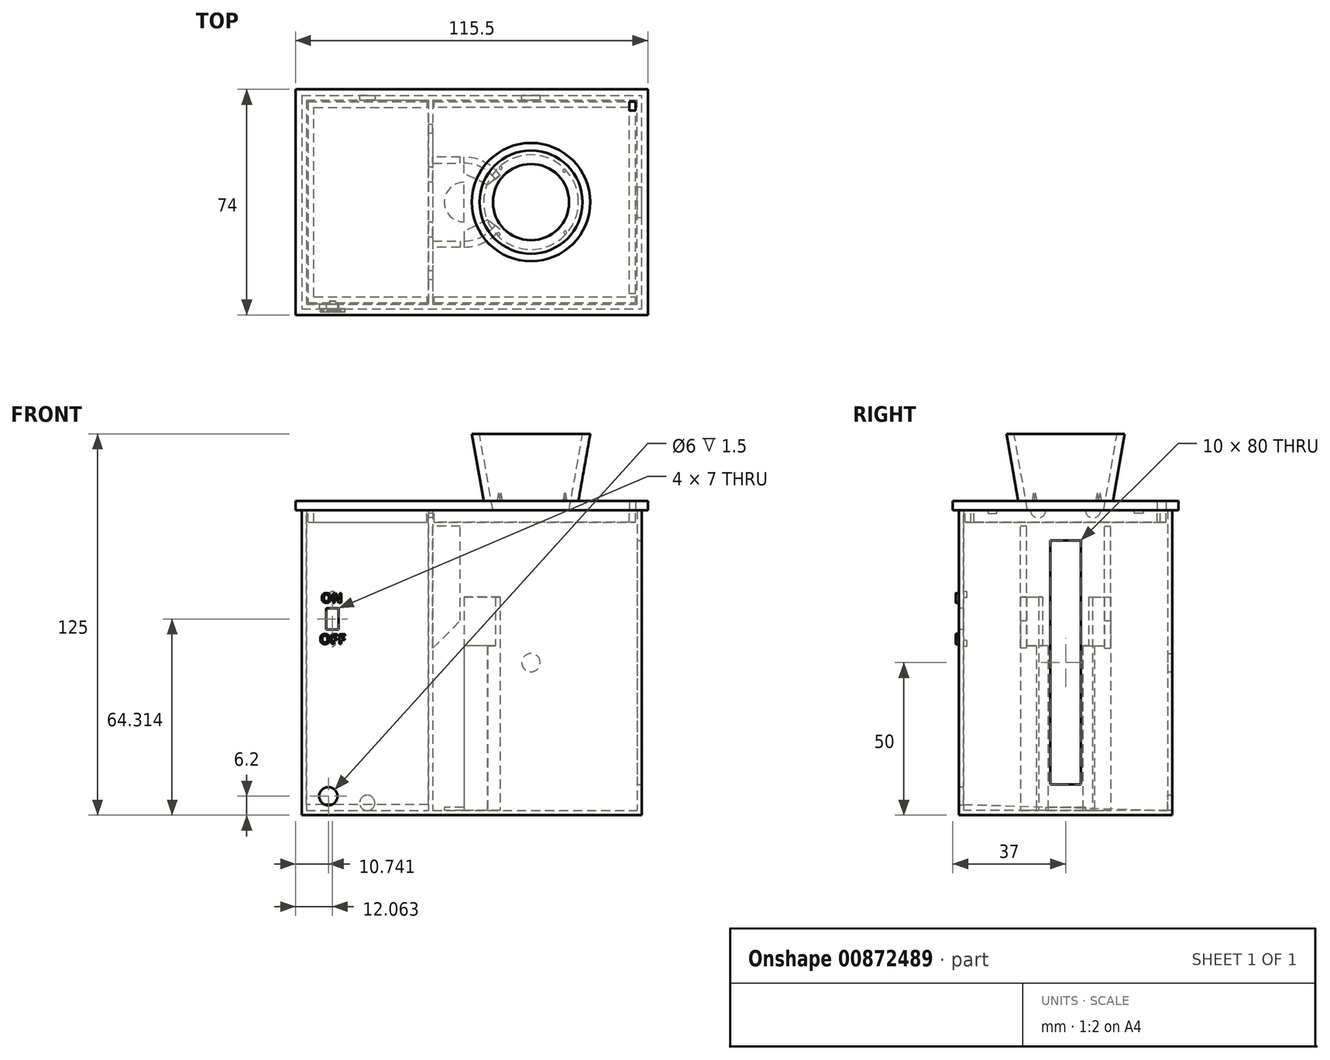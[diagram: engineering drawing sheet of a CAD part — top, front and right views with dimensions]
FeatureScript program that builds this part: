
annotation { "Feature Type Name" : "Feature", "Feature Type Description" : "" }
export const myFeature = defineFeature(function(context is Context, id is Id, definition is map)
    precondition{}
    {
        {
            var Q0;
            Q0=qCreatedBy(makeId("Top.planeOp"),FACE);
            var sketch = newSketch(context, id + "F0", { "sketchPlane" : qUnion([Q0])});
            skLineSegment(sketch, "E0.bottom", {"start": v(-33.7, 35) * mm, "end": v(36.3, 35) * mm});
            skLineSegment(sketch, "E0.left", {"start": v(-33.7, 35) * mm, "end": v(-33.7, 0) * mm});
            skLineSegment(sketch, "E0.right", {"start": v(36.3, 35) * mm, "end": v(36.3, 0) * mm});
            skLineSegment(sketch, "E1.MirrorCS", {"start": v(-33.7, -35) * mm, "end": v(-33.7, 0) * mm});
            skLineSegment(sketch, "E2.MirrorCS", {"start": v(-33.7, -35) * mm, "end": v(36.3, -35) * mm});
            skLineSegment(sketch, "E3.MirrorCS", {"start": v(36.3, -35) * mm, "end": v(36.3, 0) * mm});
            skSolve(sketch);
        }
        {
            var Q0;
            Q0 = qSketchRegion(id + "F0", true);
            extrude(context, id + "F1", {"entities" : qUnion([Q0]), "depth" : 100 * mm, "offsetDistance" : 25 * mm});
        }
        {
            var Q0;
            Q0=makeQuery(id+"F1.opExtrude","CAP_FACE",FACE,{"disambiguationData":[OSD([sQuery(id+"F0.wireOp",EDGE,"E0.bottom"),sQuery(id+"F0.wireOp",EDGE,"E0.left"),sQuery(id+"F0.wireOp",EDGE,"E0.right"),sQuery(id+"F0.wireOp",EDGE,"E1.MirrorCS"),sQuery(id+"F0.wireOp",EDGE,"E2.MirrorCS"),sQuery(id+"F0.wireOp",EDGE,"E3.MirrorCS")])],"isStart":false});
            shell(context, id + "F2", {"entities" : qUnion([Q0]), "thickness" : 1.5 * mm});
        }
        {
            var Q0;
            Q0=makeQuery(id+"F1.opExtrude","SWEPT_FACE",FACE,{"disambiguationData":[OSD([sQuery(id+"F0.wireOp",EDGE,"E0.right"),sQuery(id+"F0.wireOp",EDGE,"E3.MirrorCS")])]});
            var sketch = newSketch(context, id + "F3", { "sketchPlane" : qUnion([Q0])});
            skLineSegment(sketch, "E4", {"start": v(0, 10) * mm, "end": v(5, 10) * mm});
            skLineSegment(sketch, "E5.bottom", {"start": v(5, 10) * mm, "end": v(-5, 10) * mm});
            skLineSegment(sketch, "E5.top", {"start": v(5, 90) * mm, "end": v(-5, 90) * mm});
            skLineSegment(sketch, "E5.left", {"start": v(5, 10) * mm, "end": v(5, 90) * mm});
            skLineSegment(sketch, "E5.right", {"start": v(-5, 10) * mm, "end": v(-5, 90) * mm});
            skSolve(sketch);
        }
        {
            var Q0;
            Q0=makeQuery(id+"F3.imprint","IMPRINT",FACE,{"disambiguationData":[TD([[makeQuery(id+"F3.imprint","IMPRINT",EDGE,{"derivedFrom":sQuery(id+"F3.wireOp",EDGE,"E5.top")}),1.0]])]});
            extrude(context, id + "F4", {"entities" : qUnion([Q0]), "operationType" : NewBodyOperationType.REMOVE, "oppositeDirection" : true, "depth" : 25 * mm, "offsetDistance" : 25 * mm});
        }
        {
            var Q0;
            Q0=makeQuery(id+"F1.opExtrude","SWEPT_FACE",FACE,{"disambiguationData":[OSD([sQuery(id+"F0.wireOp",EDGE,"E0.bottom")])]});
            var sketch = newSketch(context, id + "F5", { "sketchPlane" : qUnion([Q0])});
            skCircle(sketch, "E6", {"center": v(0, 50) * mm, "radius": 3 * mm});
            skSolve(sketch);
        }
        {
            var Q0;
            Q0 = qSketchRegion(id + "F5", true);
            extrude(context, id + "F6", {"entities" : qUnion([Q0]), "operationType" : NewBodyOperationType.REMOVE, "oppositeDirection" : true, "depth" : 25 * mm, "offsetDistance" : 25 * mm});
        }
        {
            var Q0;
            Q0=makeQuery(id+"F1.opExtrude","SWEPT_FACE",FACE,{"disambiguationData":[OSD([sQuery(id+"F0.wireOp",EDGE,"E0.left"),sQuery(id+"F0.wireOp",EDGE,"E1.MirrorCS")])]});
            var sketch = newSketch(context, id + "F7", { "sketchPlane" : qUnion([Q0])});
            skCircle(sketch, "E7", {"center": v(-9, 100) * mm, "radius": 2.5 * mm});
            skCircle(sketch, "E8", {"center": v(9, 100) * mm, "radius": 2.5 * mm});
            skLineSegment(sketch, "E9", {"start": v(0, 100) * mm, "end": v(0, 73.59) * mm});
            skLineSegment(sketch, "E10", {"start": v(-35, 100) * mm, "end": v(-35, 0) * mm});
            skLineSegment(sketch, "E11", {"start": v(-35, 0) * mm, "end": v(35, 0) * mm});
            skLineSegment(sketch, "E12", {"start": v(35, 0) * mm, "end": v(35, 100) * mm});
            skLineSegment(sketch, "E13.0", {"start": v(33.5, 1.5) * mm, "end": v(33.5, 100) * mm});
            skLineSegment(sketch, "E13.1", {"start": v(-33.5, 1.5) * mm, "end": v(33.5, 1.5) * mm});
            skLineSegment(sketch, "E13.2", {"start": v(-33.5, 100) * mm, "end": v(-33.5, 1.5) * mm});
            skLineSegment(sketch, "E14", {"start": v(-33.5, 100) * mm, "end": v(-35, 100) * mm});
            skLineSegment(sketch, "E15", {"start": v(33.5, 100) * mm, "end": v(35, 100) * mm});
            skLineSegment(sketch, "E16", {"start": v(-25.5, 100) * mm, "end": v(-25.5, 99) * mm});
            skLineSegment(sketch, "E17", {"start": v(-25.5, 99) * mm, "end": v(-22.5, 99) * mm});
            skLineSegment(sketch, "E18", {"start": v(-22.5, 99) * mm, "end": v(-22.5, 100) * mm});
            skLineSegment(sketch, "E19.MirrorCS", {"start": v(22.5, 99) * mm, "end": v(22.5, 100) * mm});
            skLineSegment(sketch, "E20.MirrorCS", {"start": v(25.5, 99) * mm, "end": v(22.5, 99) * mm});
            skLineSegment(sketch, "E21.MirrorCS", {"start": v(25.5, 100) * mm, "end": v(25.5, 99) * mm});
            skSolve(sketch);
        }
        {
            var Q0;
            {var subQ0=sQuery(id+"F7.wireOp",EDGE,"E7");var subQ1=makeQuery(id+"F1.opExtrude","CAP_EDGE",EDGE,{"disambiguationData":[OSD([sQuery(id+"F0.wireOp",EDGE,"E0.left"),sQuery(id+"F0.wireOp",EDGE,"E1.MirrorCS")])],"isStart":false});var subQ2=makeQuery(id+"F7.imprint","INTERSECT",VERTEX,{"disambiguationData":[OD(0.0)],"derivedFrom":[subQ1,subQ0]});Q0=makeQuery(id+"F7.imprint","IMPRINT",FACE,{"disambiguationData":[TD([[makeQuery(id+"F7.imprint","IMPRINT",EDGE,{"disambiguationData":[TD([[subQ2,-1.0]])],"derivedFrom":subQ0}),1.0]])]});}
            var Q1;
            {var subQ0=sQuery(id+"F7.wireOp",EDGE,"E8");var subQ1=makeQuery(id+"F1.opExtrude","CAP_EDGE",EDGE,{"disambiguationData":[OSD([sQuery(id+"F0.wireOp",EDGE,"E0.left"),sQuery(id+"F0.wireOp",EDGE,"E1.MirrorCS")])],"isStart":false});var subQ2=makeQuery(id+"F7.imprint","INTERSECT",VERTEX,{"disambiguationData":[OD(0.0)],"derivedFrom":[subQ1,subQ0]});Q1=makeQuery(id+"F7.imprint","IMPRINT",FACE,{"disambiguationData":[TD([[makeQuery(id+"F7.imprint","IMPRINT",EDGE,{"disambiguationData":[TD([[subQ2,1.0]])],"derivedFrom":subQ0}),1.0]])]});}
            var Q2;
            {var subQ0=sQuery(id+"F7.wireOp",EDGE,"E16");Q2=makeQuery(id+"F7.imprint","IMPRINT",FACE,{"disambiguationData":[TD([[makeQuery(id+"F7.imprint","IMPRINT",EDGE,{"derivedFrom":subQ0}),1.0]])]});}
            var Q3;
            {var subQ0=sQuery(id+"F7.wireOp",EDGE,"E19.MirrorCS");Q3=makeQuery(id+"F7.imprint","IMPRINT",FACE,{"disambiguationData":[TD([[makeQuery(id+"F7.imprint","IMPRINT",EDGE,{"derivedFrom":subQ0}),-1.0]])]});}
            extrude(context, id + "F8", {"entities" : qUnion([Q0, Q1, Q2, Q3]), "operationType" : NewBodyOperationType.REMOVE, "oppositeDirection" : true, "depth" : 25 * mm, "offsetDistance" : 25 * mm});
        }
        {
            var Q0;
            Q0=makeQuery(id+"F7.imprint","IMPRINT",FACE,{"disambiguationData":[TD([[makeQuery(id+"F7.imprint","IMPRINT",EDGE,{"derivedFrom":sQuery(id+"F7.wireOp",EDGE,"E10")}),1.0]])]});
            extrude(context, id + "F9", {"entities" : qUnion([Q0]), "operationType" : NewBodyOperationType.ADD, "depth" : 40 * mm, "offsetDistance" : 25 * mm});
        }
        {
            var Q0;
            Q0=makeQuery(id+"F9.opExtrude","CAP_FACE",FACE,{"disambiguationData":[OSD([sQuery(id+"F7.wireOp",EDGE,"E10"),sQuery(id+"F7.wireOp",EDGE,"E11"),sQuery(id+"F7.wireOp",EDGE,"E12"),sQuery(id+"F7.wireOp",EDGE,"E13.0"),sQuery(id+"F7.wireOp",EDGE,"E13.1"),sQuery(id+"F7.wireOp",EDGE,"E13.2"),sQuery(id+"F7.wireOp",EDGE,"E14"),sQuery(id+"F7.wireOp",EDGE,"E15")])],"isStart":false});
            var sketch = newSketch(context, id + "F10", { "sketchPlane" : qUnion([Q0])});
            skLineSegment(sketch, "E22", {"start": v(-35, 100) * mm, "end": v(35, 100) * mm});
            skLineSegment(sketch, "E23", {"start": v(35, 100) * mm, "end": v(35, 0) * mm});
            skLineSegment(sketch, "E24", {"start": v(35, 0) * mm, "end": v(-35, 0) * mm});
            skLineSegment(sketch, "E25", {"start": v(-35, 0) * mm, "end": v(-35, 100) * mm});
            skSolve(sketch);
        }
        {
            var Q0;
            Q0 = qSketchRegion(id + "F10", true);
            extrude(context, id + "F11", {"entities" : qUnion([Q0]), "operationType" : NewBodyOperationType.ADD, "depth" : 1.5 * mm, "offsetDistance" : 25 * mm});
        }
        {
            var Q0;
            Q0=makeQuery(id+"F11.boolean.opBoolean","MERGE",FACE,{"derivedFrom":[makeQuery(id+"F9.boolean.opBoolean","MERGE",FACE,{"derivedFrom":[makeQuery(id+"F1.opExtrude","SWEPT_FACE",FACE,{"disambiguationData":[OSD([sQuery(id+"F0.wireOp",EDGE,"E2.MirrorCS")])]}),makeQuery(id+"F9.opExtrude","SWEPT_FACE",FACE,{"disambiguationData":[OSD([sQuery(id+"F7.wireOp",EDGE,"E12")])]})]}),makeQuery(id+"F11.opExtrude","SWEPT_FACE",FACE,{"disambiguationData":[OSD([sQuery(id+"F10.wireOp",EDGE,"E23")])]})]});
            var sketch = newSketch(context, id + "F12", { "sketchPlane" : qUnion([Q0])});
            skCircle(sketch, "E26", {"center": v(-66.47, 6.2) * mm, "radius": 3 * mm});
            skSolve(sketch);
        }
        {
            var Q0;
            Q0=makeQuery(id+"F12.imprint","IMPRINT",FACE,{"disambiguationData":[TD([[makeQuery(id+"F12.imprint","IMPRINT",EDGE,{"derivedFrom":sQuery(id+"F12.wireOp",EDGE,"E26")}),1.0]])]});
            extrude(context, id + "F13", {"entities" : qUnion([Q0]), "operationType" : NewBodyOperationType.REMOVE, "oppositeDirection" : true, "depth" : 25 * mm, "offsetDistance" : 25 * mm});
        }
        {
            var Q0;
            Q0=makeQuery(id+"F2.opShell","OFFSET_FACE",FACE,{"disambiguationData":[OSD([sQuery(id+"F0.wireOp",EDGE,"E0.bottom"),sQuery(id+"F0.wireOp",EDGE,"E0.left"),sQuery(id+"F0.wireOp",EDGE,"E0.right"),sQuery(id+"F0.wireOp",EDGE,"E1.MirrorCS"),sQuery(id+"F0.wireOp",EDGE,"E2.MirrorCS"),sQuery(id+"F0.wireOp",EDGE,"E3.MirrorCS")])]});
            var sketch = newSketch(context, id + "F14", { "sketchPlane" : qUnion([Q0])});
            skArc(sketch, "E27", {"start": v(-32.2, -7.58) * mm, "mid": v(-21.96, -12.75) * mm, "end": v(-11.7, -7.58) * mm});
            skLineSegment(sketch, "E28", {"start": v(-32.2, 0) * mm, "end": v(-11.7, 0) * mm});
            skLineSegment(sketch, "E29", {"start": v(-11.7, 0) * mm, "end": v(-11.7, 7.58) * mm});
            skLineSegment(sketch, "E30", {"start": v(-11.7, 7.58) * mm, "end": v(-11.7, -7.58) * mm});
            skLineSegment(sketch, "E31", {"start": v(-32.2, 7.58) * mm, "end": v(-32.2, -7.58) * mm});
            skArc(sketch, "E32.trimOffspring", {"start": v(-11.7, 7.58) * mm, "mid": v(-21.96, 12.75) * mm, "end": v(-32.2, 7.58) * mm});
            skCircle(sketch, "E33", {"center": v(-21.96, 0) * mm, "radius": 6.5 * mm});
            skArc(sketch, "E34.0", {"start": v(-9.7, 8.22) * mm, "mid": v(-21.62, 14.75) * mm, "end": v(-33.82, 8.77) * mm});
            skLineSegment(sketch, "E34.1", {"start": v(-9.7, 8.22) * mm, "end": v(-9.7, -8.22) * mm});
            skArc(sketch, "E34.2", {"start": v(-33.82, -8.77) * mm, "mid": v(-21.62, -14.75) * mm, "end": v(-9.7, -8.22) * mm});
            skLineSegment(sketch, "E35", {"start": v(-11.7, 7.58) * mm, "end": v(-21.96, 0) * mm});
            skLineSegment(sketch, "E36", {"start": v(-11.7, 7.58) * mm, "end": v(-10.1, 8.77) * mm});
            skLineSegment(sketch, "E37", {"start": v(-21.96, 0) * mm, "end": v(-21.96, 14.75) * mm});
            skLineSegment(sketch, "E38", {"start": v(-21.96, 0) * mm, "end": v(-21.96, -14.75) * mm});
            skLineSegment(sketch, "E39", {"start": v(-21.96, 0) * mm, "end": v(-11.7, -7.58) * mm});
            skLineSegment(sketch, "E40", {"start": v(-11.7, -7.58) * mm, "end": v(-10.1, -8.77) * mm});
            skLineSegment(sketch, "E41", {"start": v(-14.21, -5.73) * mm, "end": v(-21.96, -9.63) * mm});
            skLineSegment(sketch, "E42", {"start": v(-14.28, 5.68) * mm, "end": v(-21.96, 9.4) * mm});
            skSolve(sketch);
        }
        {
            var Q0;
            {var subQ1=sQuery(id+"F14.wireOp",EDGE,"E28");var subQ3=sQuery(id+"F14.wireOp",EDGE,"E33");var subQ4=makeQuery(id+"F14.imprint","INTERSECT",VERTEX,{"disambiguationData":[OD(0.0)],"derivedFrom":[subQ1,subQ3]});Q0=makeQuery(id+"F14.imprint","IMPRINT",FACE,{"disambiguationData":[TD([[makeQuery(id+"F14.imprint","IMPRINT",EDGE,{"disambiguationData":[TD([[subQ4,1.0]])],"derivedFrom":subQ3}),1.0]])]});}
            var Q1;
            {var subQ1=sQuery(id+"F14.wireOp",EDGE,"E28");var subQ3=sQuery(id+"F14.wireOp",EDGE,"E33");var subQ4=makeQuery(id+"F14.imprint","INTERSECT",VERTEX,{"disambiguationData":[OD(0.0)],"derivedFrom":[subQ1,subQ3]});Q1=makeQuery(id+"F14.imprint","IMPRINT",FACE,{"disambiguationData":[TD([[makeQuery(id+"F14.imprint","IMPRINT",EDGE,{"disambiguationData":[TD([[subQ4,-1.0]])],"derivedFrom":subQ3}),1.0]])]});}
            extrude(context, id + "F15", {"entities" : qUnion([Q0, Q1]), "operationType" : NewBodyOperationType.ADD, "depth" : 1 * mm, "offsetDistance" : 25 * mm});
        }
        {
            var Q0;
            {var subQ5=sQuery(id+"F14.wireOp",EDGE,"E41");Q0=makeQuery(id+"F14.imprint","IMPRINT",FACE,{"disambiguationData":[TD([[makeQuery(id+"F14.imprint","IMPRINT",EDGE,{"derivedFrom":subQ5}),1.0]])]});}
            var Q1;
            {var subQ5=sQuery(id+"F14.wireOp",EDGE,"E42");Q1=makeQuery(id+"F14.imprint","IMPRINT",FACE,{"disambiguationData":[TD([[makeQuery(id+"F14.imprint","IMPRINT",EDGE,{"derivedFrom":subQ5}),-1.0]])]});}
            var Q2;
            {var subQ0=sQuery(id+"F14.wireOp",EDGE,"E36");Q2=makeQuery(id+"F14.imprint","IMPRINT",FACE,{"disambiguationData":[TD([[makeQuery(id+"F14.imprint","IMPRINT",EDGE,{"derivedFrom":subQ0}),1.0]])]});}
            var Q3;
            {var subQ0=sQuery(id+"F14.wireOp",EDGE,"E40");Q3=makeQuery(id+"F14.imprint","IMPRINT",FACE,{"disambiguationData":[TD([[makeQuery(id+"F14.imprint","IMPRINT",EDGE,{"derivedFrom":subQ0}),-1.0]])]});}
            extrude(context, id + "F16", {"entities" : qUnion([Q0, Q1, Q2, Q3]), "operationType" : NewBodyOperationType.ADD, "depth" : 54 * mm, "offsetDistance" : 25 * mm});
        }
        {
            var Q0;
            {var subQ0=sQuery(id+"F14.wireOp",EDGE,"E36");Q0=makeQuery(id+"F14.imprint","IMPRINT",FACE,{"disambiguationData":[TD([[makeQuery(id+"F14.imprint","IMPRINT",EDGE,{"derivedFrom":subQ0}),1.0]])]});}
            var Q1;
            {var subQ0=sQuery(id+"F14.wireOp",EDGE,"E40");Q1=makeQuery(id+"F14.imprint","IMPRINT",FACE,{"disambiguationData":[TD([[makeQuery(id+"F14.imprint","IMPRINT",EDGE,{"derivedFrom":subQ0}),-1.0]])]});}
            extrude(context, id + "F17", {"entities" : qUnion([Q0, Q1]), "operationType" : NewBodyOperationType.ADD, "depth" : 70 * mm, "offsetDistance" : 25 * mm});
        }
        {
            var Q0;
            Q0=makeQuery(id+"F2.opShell","OFFSET_FACE",FACE,{"disambiguationData":[OSD([sQuery(id+"F0.wireOp",EDGE,"E0.left"),sQuery(id+"F0.wireOp",EDGE,"E1.MirrorCS")])]});
            var sketch = newSketch(context, id + "F18", { "sketchPlane" : qUnion([Q0])});
            skLineSegment(sketch, "E43", {"start": v(0, 100) * mm, "end": v(0, 54.72) * mm});
            skLineSegment(sketch, "E44", {"start": v(0, 54.72) * mm, "end": v(12.75, 54.72) * mm});
            skLineSegment(sketch, "E45", {"start": v(0, 54.72) * mm, "end": v(-12.75, 54.72) * mm});
            skLineSegment(sketch, "E46.bottom", {"start": v(-12.75, 54.72) * mm, "end": v(-14.75, 54.72) * mm});
            skLineSegment(sketch, "E46.top", {"start": v(-12.75, 94.72) * mm, "end": v(-14.75, 94.72) * mm});
            skLineSegment(sketch, "E46.left", {"start": v(-12.75, 54.72) * mm, "end": v(-12.75, 94.72) * mm});
            skLineSegment(sketch, "E46.right", {"start": v(-14.75, 54.72) * mm, "end": v(-14.75, 94.72) * mm});
            skLineSegment(sketch, "E47.bottom", {"start": v(12.75, 54.72) * mm, "end": v(14.75, 54.72) * mm});
            skLineSegment(sketch, "E47.top", {"start": v(12.75, 94.72) * mm, "end": v(14.75, 94.72) * mm});
            skLineSegment(sketch, "E47.left", {"start": v(12.75, 54.72) * mm, "end": v(12.75, 94.72) * mm});
            skLineSegment(sketch, "E47.right", {"start": v(14.75, 54.72) * mm, "end": v(14.75, 94.72) * mm});
            skSolve(sketch);
        }
        {
            var Q0;
            Q0=makeQuery(id+"F18.imprint","IMPRINT",FACE,{"disambiguationData":[TD([[makeQuery(id+"F18.imprint","IMPRINT",EDGE,{"derivedFrom":sQuery(id+"F18.wireOp",EDGE,"E46.bottom")}),-1.0]])]});
            var Q1;
            Q1=makeQuery(id+"F18.imprint","IMPRINT",FACE,{"disambiguationData":[TD([[makeQuery(id+"F18.imprint","IMPRINT",EDGE,{"derivedFrom":sQuery(id+"F18.wireOp",EDGE,"E47.bottom")}),1.0]])]});
            extrude(context, id + "F19", {"entities" : qUnion([Q0, Q1]), "operationType" : NewBodyOperationType.ADD, "depth" : 9 * mm, "offsetDistance" : 25 * mm});
        }
        {
            var Q0;
            Q0=makeQuery(id+"F19.opExtrude","CAP_EDGE",EDGE,{"disambiguationData":[OSD([sQuery(id+"F18.wireOp",EDGE,"E46.bottom")])],"isStart":false});
            var Q1;
            Q1=makeQuery(id+"F19.opExtrude","CAP_EDGE",EDGE,{"disambiguationData":[OSD([sQuery(id+"F18.wireOp",EDGE,"E47.bottom")])],"isStart":false});
            chamfer(context, id + "F20", {"entities" : qUnion([Q0, Q1]), "width" : 9 * mm, "tangentPropagation" : true});
        }
        {
            var Q0;
            Q0=makeQuery(id+"F9.opExtrude","SWEPT_FACE",FACE,{"disambiguationData":[OSD([sQuery(id+"F7.wireOp",EDGE,"E13.2")])]});
            var sketch = newSketch(context, id + "F21", { "sketchPlane" : qUnion([Q0])});
            skLineSegment(sketch, "E48", {"start": v(-53.7, 1.5) * mm, "end": v(-53.7, 4) * mm});
            skCircle(sketch, "E49", {"center": v(-53.7, 4) * mm, "radius": 2.5 * mm});
            skSolve(sketch);
        }
        {
            var Q0;
            Q0=makeQuery(id+"F21.imprint","IMPRINT",FACE,{"disambiguationData":[TD([[makeQuery(id+"F21.imprint","IMPRINT",EDGE,{"derivedFrom":sQuery(id+"F21.wireOp",EDGE,"E49")}),1.0]])]});
            extrude(context, id + "F22", {"entities" : qUnion([Q0]), "operationType" : NewBodyOperationType.REMOVE, "oppositeDirection" : true, "depth" : 25 * mm, "offsetDistance" : 25 * mm});
        }
        {
            var Q0;
            Q0=makeQuery(id+"F1.opExtrude","SWEPT_FACE",FACE,{"disambiguationData":[OSD([sQuery(id+"F0.wireOp",EDGE,"E0.left"),sQuery(id+"F0.wireOp",EDGE,"E1.MirrorCS")])]});
            var sketch = newSketch(context, id + "F23", { "sketchPlane" : qUnion([Q0])});
            skLineSegment(sketch, "E50", {"start": v(-33.5, 1.5) * mm, "end": v(33.5, 1.5) * mm});
            skLineSegment(sketch, "E51", {"start": v(33.5, 1.5) * mm, "end": v(33.5, 3.5) * mm});
            skLineSegment(sketch, "E52", {"start": v(33.5, 3.5) * mm, "end": v(-33.5, 1.5) * mm});
            skSolve(sketch);
        }
        {
            var Q0;
            Q0=makeQuery(id+"F23.imprint","IMPRINT",FACE,{"disambiguationData":[TD([[makeQuery(id+"F23.imprint","IMPRINT",EDGE,{"derivedFrom":sQuery(id+"F23.wireOp",EDGE,"E50")}),1.0]])]});
            var Q1;
            Q1=makeQuery(id+"F9.opExtrude","SWEPT_EDGE",EDGE,{"disambiguationData":[OSD([sQuery(id+"F7.wireOp",EDGE,"E13.0"),sQuery(id+"F7.wireOp",EDGE,"E13.1")])]});
            sweep(context, id + "F24", {"operationType" : NewBodyOperationType.ADD, "profiles" : qUnion([Q0]), "path" : qUnion([Q1])});
        }
        {
            var Q0;
            Q0=makeQuery(id+"F11.boolean.opBoolean","MERGE",FACE,{"derivedFrom":[makeQuery(id+"F9.boolean.opBoolean","MERGE",FACE,{"derivedFrom":[makeQuery(id+"F1.opExtrude","SWEPT_FACE",FACE,{"disambiguationData":[OSD([sQuery(id+"F0.wireOp",EDGE,"E2.MirrorCS")])]}),makeQuery(id+"F9.opExtrude","SWEPT_FACE",FACE,{"disambiguationData":[OSD([sQuery(id+"F7.wireOp",EDGE,"E12")])]})]}),makeQuery(id+"F11.opExtrude","SWEPT_FACE",FACE,{"disambiguationData":[OSD([sQuery(id+"F10.wireOp",EDGE,"E23")])]})]});
            var sketch = newSketch(context, id + "F25", { "sketchPlane" : qUnion([Q0])});
            skLineSegment(sketch, "E53.bottom", {"start": v(-67.15, 67.81) * mm, "end": v(-63.15, 67.81) * mm});
            skLineSegment(sketch, "E53.top", {"start": v(-67.15, 60.81) * mm, "end": v(-63.15, 60.81) * mm});
            skLineSegment(sketch, "E53.left", {"start": v(-67.15, 67.81) * mm, "end": v(-67.15, 60.81) * mm});
            skLineSegment(sketch, "E53.right", {"start": v(-63.15, 67.81) * mm, "end": v(-63.15, 60.81) * mm});
            skText(sketch, "E54", { "text": "ON", "fontName": "OpenSans-Bold.ttf"});
            skText(sketch, "E55", { "text": "OFF", "fontName": "OpenSans-Bold.ttf"});
            const initialGuessF25  = {"E54": [-0.06887, 0.06965, 1, 0, 0.00318], "E55": [-0.06941, 0.0561, 1, 0, 0.00328]};
            skSetInitialGuess(sketch, initialGuessF25);
            skSolve(sketch);
        }
        {
            var Q0;
            Q0=makeQuery(id+"F25.imprint","IMPRINT",FACE,{"disambiguationData":[TD([[makeQuery(id+"F25.imprint","IMPRINT",EDGE,{"derivedFrom":sQuery(id+"F25.wireOp",EDGE,"E53.bottom")}),-1.0]])]});
            extrude(context, id + "F26", {"entities" : qUnion([Q0]), "operationType" : NewBodyOperationType.REMOVE, "oppositeDirection" : true, "depth" : 25 * mm, "offsetDistance" : 25 * mm});
        }
        {
            var Q0;
            Q0=makeQuery(id+"F9.opExtrude","SWEPT_FACE",FACE,{"disambiguationData":[OSD([sQuery(id+"F7.wireOp",EDGE,"E13.0")])]});
            var sketch = newSketch(context, id + "F27", { "sketchPlane" : qUnion([Q0])});
            skLineSegment(sketch, "E56", {"start": v(65.15, 67.81) * mm, "end": v(65.15, 72.31) * mm});
            skCircle(sketch, "E57", {"center": v(65.15, 72.31) * mm, "radius": 1 * mm});
            skLineSegment(sketch, "E58", {"start": v(67.15, 64.31) * mm, "end": v(68.8, 64.31) * mm});
            skCircle(sketch, "E59.MirrorC", {"center": v(65.15, 56.31) * mm, "radius": 1 * mm});
            skSolve(sketch);
        }
        {
            var Q0;
            Q0 = qSketchRegion(id + "F27", true);
            extrude(context, id + "F28", {"entities" : qUnion([Q0]), "operationType" : NewBodyOperationType.ADD, "depth" : 1 * mm, "offsetDistance" : 25 * mm});
        }
        {
            var Q0;
            Q0=makeQuery(id+"F25.imprint","IMPRINT",FACE,{"disambiguationData":[TD([[makeQuery(id+"F25.imprint","IMPRINT",EDGE,{"derivedFrom":sQuery(id+"F25.wireOp",EDGE,"E54.sketch_text.stroke-0")}),-1.0]])]});
            var Q1;
            Q1=makeQuery(id+"F25.imprint","IMPRINT",FACE,{"disambiguationData":[TD([[makeQuery(id+"F25.imprint","IMPRINT",EDGE,{"derivedFrom":sQuery(id+"F25.wireOp",EDGE,"E54.sketch_text.stroke-14")}),-1.0]])]});
            var Q2;
            Q2=makeQuery(id+"F25.imprint","IMPRINT",FACE,{"disambiguationData":[TD([[makeQuery(id+"F25.imprint","IMPRINT",EDGE,{"derivedFrom":sQuery(id+"F25.wireOp",EDGE,"E55.sketch_text.stroke-0")}),-1.0]])]});
            var Q3;
            Q3=makeQuery(id+"F25.imprint","IMPRINT",FACE,{"disambiguationData":[TD([[makeQuery(id+"F25.imprint","IMPRINT",EDGE,{"derivedFrom":sQuery(id+"F25.wireOp",EDGE,"E55.sketch_text.stroke-14")}),-1.0]])]});
            var Q4;
            Q4=makeQuery(id+"F25.imprint","IMPRINT",FACE,{"disambiguationData":[TD([[makeQuery(id+"F25.imprint","IMPRINT",EDGE,{"derivedFrom":sQuery(id+"F25.wireOp",EDGE,"E55.sketch_text.stroke-24")}),-1.0]])]});
            extrude(context, id + "F29", {"entities" : qUnion([Q0, Q1, Q2, Q3, Q4]), "operationType" : NewBodyOperationType.ADD, "depth" : 1 * mm, "offsetDistance" : 25 * mm});
        }
        {
            var Q0;
            {var subQ0=sQuery(id+"F0.wireOp",EDGE,"E3.MirrorCS");var subQ1=sQuery(id+"F0.wireOp",EDGE,"E0.right");var subQ2=sQuery(id+"F0.wireOp",EDGE,"E0.bottom");var subQ3=sQuery(id+"F0.wireOp",EDGE,"E1.MirrorCS");var subQ4=sQuery(id+"F0.wireOp",EDGE,"E0.left");var subQ5=sQuery(id+"F0.wireOp",EDGE,"E2.MirrorCS");Q0=makeQuery(id+"F11.boolean.opBoolean","MERGE",FACE,{"derivedFrom":[makeQuery(id+"F9.boolean.opBoolean","MERGE",FACE,{"derivedFrom":[makeQuery(id+"F8.boolean.opBoolean","SPLIT",FACE,{"disambiguationData":[TD([makeQuery(id+"F1.opExtrude","SWEPT_FACE",FACE,{"disambiguationData":[OSD([subQ2])]}),makeQuery(id+"F1.opExtrude","SWEPT_FACE",FACE,{"disambiguationData":[OSD([subQ4,subQ3])]}),makeQuery(id+"F1.opExtrude","SWEPT_FACE",FACE,{"disambiguationData":[OSD([subQ1,subQ0])]}),makeQuery(id+"F1.opExtrude","SWEPT_FACE",FACE,{"disambiguationData":[OSD([subQ5])]}),makeQuery(id+"F2.opShell","OFFSET_FACE",FACE,{"disambiguationData":[OSD([subQ2])]}),makeQuery(id+"F2.opShell","OFFSET_FACE",FACE,{"disambiguationData":[OSD([subQ4,subQ3])]}),makeQuery(id+"F2.opShell","OFFSET_FACE",FACE,{"disambiguationData":[OSD([subQ1,subQ0])]}),makeQuery(id+"F2.opShell","OFFSET_FACE",FACE,{"disambiguationData":[OSD([subQ5])]}),makeQuery(id+"F8.opExtrude","SWEPT_FACE",FACE,{"disambiguationData":[OSD([sQuery(id+"F7.wireOp",EDGE,"E16")])]}),makeQuery(id+"F8.opExtrude","SWEPT_FACE",FACE,{"disambiguationData":[OSD([sQuery(id+"F7.wireOp",EDGE,"E21.MirrorCS")])]})])],"derivedFrom":makeQuery(id+"F1.opExtrude","CAP_FACE",FACE,{"disambiguationData":[OSD([subQ2,subQ4,subQ1,subQ3,subQ5,subQ0])],"isStart":false})}),makeQuery(id+"F9.opExtrude","SWEPT_FACE",FACE,{"disambiguationData":[OSD([sQuery(id+"F7.wireOp",EDGE,"E14")])]}),makeQuery(id+"F9.opExtrude","SWEPT_FACE",FACE,{"disambiguationData":[OSD([sQuery(id+"F7.wireOp",EDGE,"E15")])]})]}),makeQuery(id+"F11.opExtrude","SWEPT_FACE",FACE,{"disambiguationData":[OSD([sQuery(id+"F10.wireOp",EDGE,"E22")])]})]});}
            var sketch = newSketch(context, id + "F30", { "sketchPlane" : qUnion([Q0])});
            skLineSegment(sketch, "E60", {"start": v(36.3, 35) * mm, "end": v(36.3, 37) * mm, "construction": true});
            skLineSegment(sketch, "E61", {"start": v(36.3, 37) * mm, "end": v(38.3, 37) * mm});
            skLineSegment(sketch, "E62", {"start": v(-75.2, -35) * mm, "end": v(-77.2, -35) * mm, "construction": true});
            skLineSegment(sketch, "E63", {"start": v(-77.2, -35) * mm, "end": v(-77.2, -37) * mm});
            skLineSegment(sketch, "E64.bottom", {"start": v(-77.2, -37) * mm, "end": v(38.3, -37) * mm});
            skLineSegment(sketch, "E64.top", {"start": v(-77.2, 37) * mm, "end": v(38.3, 37) * mm});
            skLineSegment(sketch, "E64.left", {"start": v(-77.2, -37) * mm, "end": v(-77.2, 37) * mm});
            skLineSegment(sketch, "E64.right", {"start": v(38.3, -37) * mm, "end": v(38.3, 37) * mm});
            skLineSegment(sketch, "E65", {"start": v(34.8, 33.5) * mm, "end": v(34.3, 33.5) * mm, "construction": true});
            skLineSegment(sketch, "E66", {"start": v(34.3, 33.5) * mm, "end": v(34.3, 33) * mm, "construction": true});
            skLineSegment(sketch, "E67", {"start": v(-32.2, -33.5) * mm, "end": v(-32.2, -33) * mm, "construction": true});
            skLineSegment(sketch, "E68", {"start": v(-32.2, -33) * mm, "end": v(-31.7, -33) * mm, "construction": true});
            skLineSegment(sketch, "E69.bottom", {"start": v(-31.7, -33) * mm, "end": v(34.3, -33) * mm});
            skLineSegment(sketch, "E69.top", {"start": v(-31.7, 33) * mm, "end": v(34.3, 33) * mm});
            skLineSegment(sketch, "E69.left", {"start": v(-31.7, -33) * mm, "end": v(-31.7, 33) * mm});
            skLineSegment(sketch, "E69.right", {"start": v(34.3, -33) * mm, "end": v(34.3, 33) * mm});
            skLineSegment(sketch, "E70", {"start": v(-73.7, 33.5) * mm, "end": v(-73.2, 33.5) * mm, "construction": true});
            skLineSegment(sketch, "E71", {"start": v(-73.2, 33.5) * mm, "end": v(-73.2, 33) * mm, "construction": true});
            skLineSegment(sketch, "E72", {"start": v(-33.7, -33.5) * mm, "end": v(-33.7, -33) * mm, "construction": true});
            skLineSegment(sketch, "E73", {"start": v(-33.7, -33) * mm, "end": v(-34.2, -33) * mm, "construction": true});
            skLineSegment(sketch, "E74.bottom", {"start": v(-73.2, 33) * mm, "end": v(-34.2, 33) * mm});
            skLineSegment(sketch, "E74.top", {"start": v(-73.2, -33) * mm, "end": v(-34.2, -33) * mm});
            skLineSegment(sketch, "E74.left", {"start": v(-73.2, 33) * mm, "end": v(-73.2, -33) * mm});
            skLineSegment(sketch, "E74.right", {"start": v(-34.2, 33) * mm, "end": v(-34.2, -33) * mm});
            skCircle(sketch, "E75", {"center": v(0, 0) * mm, "radius": 15 * mm});
            skCircle(sketch, "E76", {"center": v(0, 0) * mm, "radius": 12.5 * mm});
            skLineSegment(sketch, "E77", {"start": v(-73.2, -33) * mm, "end": v(-73.2, -31) * mm});
            skLineSegment(sketch, "E78", {"start": v(-73.2, -31) * mm, "end": v(-34.2, -31) * mm});
            skLineSegment(sketch, "E79", {"start": v(-73.2, -33) * mm, "end": v(-71.2, -33) * mm});
            skLineSegment(sketch, "E80", {"start": v(-71.2, -33) * mm, "end": v(-71.2, 33) * mm});
            skLineSegment(sketch, "E81", {"start": v(-73.2, 33) * mm, "end": v(-73.2, 31) * mm});
            skLineSegment(sketch, "E82", {"start": v(-73.2, 31) * mm, "end": v(-34.2, 31) * mm});
            skLineSegment(sketch, "E83", {"start": v(-31.7, -33) * mm, "end": v(-31.7, -31) * mm});
            skLineSegment(sketch, "E84", {"start": v(-31.7, -31) * mm, "end": v(34.3, -31) * mm});
            skLineSegment(sketch, "E85", {"start": v(34.3, -33) * mm, "end": v(32.3, -33) * mm});
            skLineSegment(sketch, "E86", {"start": v(32.3, -33) * mm, "end": v(32.3, 33) * mm});
            skLineSegment(sketch, "E87", {"start": v(34.3, 33) * mm, "end": v(34.3, 31) * mm});
            skLineSegment(sketch, "E88", {"start": v(34.3, 31) * mm, "end": v(-31.7, 31) * mm});
            skLineSegment(sketch, "E89", {"start": v(-73.2, -31) * mm, "end": v(-73.2, -30) * mm});
            skLineSegment(sketch, "E90", {"start": v(-73.2, -30) * mm, "end": v(-71.2, -30) * mm});
            skLineSegment(sketch, "E91", {"start": v(-73.2, 31) * mm, "end": v(-73.2, 30) * mm});
            skLineSegment(sketch, "E92", {"start": v(-73.2, 30) * mm, "end": v(-71.2, 30) * mm});
            skLineSegment(sketch, "E93", {"start": v(34.3, -31) * mm, "end": v(34.3, -30) * mm});
            skLineSegment(sketch, "E94", {"start": v(34.3, -30) * mm, "end": v(32.3, -30) * mm});
            skLineSegment(sketch, "E95", {"start": v(34.3, 31) * mm, "end": v(34.3, 30) * mm});
            skLineSegment(sketch, "E96", {"start": v(34.3, 30) * mm, "end": v(32.3, 30) * mm});
            skLineSegment(sketch, "E97", {"start": v(-31.7, -31) * mm, "end": v(34.3, 33) * mm, "construction": true});
            skLineSegment(sketch, "E98", {"start": v(-31.7, 33) * mm, "end": v(34.3, -33) * mm, "construction": true});
            skCircle(sketch, "E99", {"center": v(-10.64, -10.57) * mm, "radius": 1 * mm});
            skCircle(sketch, "E100", {"center": v(11.23, -9.94) * mm, "radius": 1 * mm});
            skCircle(sketch, "E101", {"center": v(10.9, 10.31) * mm, "radius": 1 * mm});
            skCircle(sketch, "E102", {"center": v(-9.94, 11.23) * mm, "radius": 1 * mm});
            skSolve(sketch);
        }
        {
            var Q0;
            Q0=makeQuery(id+"F30.imprint","IMPRINT",FACE,{"disambiguationData":[TD([[makeQuery(id+"F30.imprint","IMPRINT",EDGE,{"derivedFrom":sQuery(id+"F30.wireOp",EDGE,"E69.bottom")}),1.0]])]});
            var Q1;
            Q1=makeQuery(id+"F30.imprint","IMPRINT",FACE,{"disambiguationData":[TD([[makeQuery(id+"F30.imprint","IMPRINT",EDGE,{"derivedFrom":sQuery(id+"F30.wireOp",EDGE,"E69.bottom")}),-1.0]])]});
            var Q2;
            {var subQ20=sQuery(id+"F10.wireOp",EDGE,"E22");Q2=makeQuery(id+"F30.imprint","IMPRINT",FACE,{"disambiguationData":[TD([[makeQuery(id+"F30.imprint","IMPRINT",EDGE,{"derivedFrom":makeQuery(id+"F11.opExtrude","CAP_EDGE",EDGE,{"disambiguationData":[OSD([subQ20])],"isStart":false})}),1.0]])]});}
            var Q3;
            {var subQ3=sQuery(id+"F30.wireOp",EDGE,"E64.bottom");Q3=makeQuery(id+"F30.imprint","IMPRINT",FACE,{"disambiguationData":[TD([[makeQuery(id+"F30.imprint","IMPRINT",EDGE,{"derivedFrom":subQ3}),1.0]])]});}
            var Q4;
            Q4=makeQuery(id+"F30.imprint","IMPRINT",FACE,{"disambiguationData":[TD([[makeQuery(id+"F30.imprint","IMPRINT",EDGE,{"derivedFrom":sQuery(id+"F30.wireOp",EDGE,"E75")}),1.0]])]});
            var Q5;
            {var subQ0=sQuery(id+"F30.wireOp",EDGE,"E74.left");Q5=makeQuery(id+"F30.imprint","IMPRINT",FACE,{"disambiguationData":[TD([[makeQuery(id+"F30.imprint","IMPRINT",EDGE,{"derivedFrom":subQ0}),1.0]])]});}
            var Q6;
            {var subQ0=sQuery(id+"F30.wireOp",EDGE,"E77");Q6=makeQuery(id+"F30.imprint","IMPRINT",FACE,{"disambiguationData":[TD([[makeQuery(id+"F30.imprint","IMPRINT",EDGE,{"derivedFrom":subQ0}),-1.0]])]});}
            var Q7;
            {var subQ0=sQuery(id+"F30.wireOp",EDGE,"E74.top");Q7=makeQuery(id+"F30.imprint","IMPRINT",FACE,{"disambiguationData":[TD([[makeQuery(id+"F30.imprint","IMPRINT",EDGE,{"derivedFrom":subQ0}),1.0]])]});}
            var Q8;
            {var subQ0=sQuery(id+"F30.wireOp",EDGE,"E78");var subQ1=sQuery(id+"F30.wireOp",EDGE,"E74.right");var subQ2=makeQuery(id+"F30.imprint","INTERSECT",VERTEX,{"derivedFrom":[subQ1,subQ0]});Q8=makeQuery(id+"F30.imprint","IMPRINT",FACE,{"disambiguationData":[TD([[makeQuery(id+"F30.imprint","IMPRINT",EDGE,{"disambiguationData":[TD([[subQ2,1.0]])],"derivedFrom":subQ1}),-1.0]])]});}
            var Q9;
            {var subQ0=sQuery(id+"F30.wireOp",EDGE,"E69.left");var subQ1=sQuery(id+"F30.wireOp",EDGE,"E69.top");var subQ2=makeQuery(id+"F30.imprint","INTERSECT",VERTEX,{"derivedFrom":[subQ1,subQ0]});Q9=makeQuery(id+"F30.imprint","IMPRINT",FACE,{"disambiguationData":[TD([[makeQuery(id+"F30.imprint","IMPRINT",EDGE,{"disambiguationData":[TD([[subQ2,-1.0]])],"derivedFrom":subQ1}),-1.0]])]});}
            var Q10;
            {var subQ0=sQuery(id+"F30.wireOp",EDGE,"E87");Q10=makeQuery(id+"F30.imprint","IMPRINT",FACE,{"disambiguationData":[TD([[makeQuery(id+"F30.imprint","IMPRINT",EDGE,{"derivedFrom":subQ0}),-1.0]])]});}
            var Q11;
            {var subQ0=sQuery(id+"F30.wireOp",EDGE,"E85");Q11=makeQuery(id+"F30.imprint","IMPRINT",FACE,{"disambiguationData":[TD([[makeQuery(id+"F30.imprint","IMPRINT",EDGE,{"derivedFrom":subQ0}),-1.0]])]});}
            var Q12;
            {var subQ1=sQuery(id+"F30.wireOp",EDGE,"E69.right");var subQ3=sQuery(id+"F30.wireOp",EDGE,"E84");var subQ4=makeQuery(id+"F30.imprint","INTERSECT",VERTEX,{"derivedFrom":[subQ1,subQ3]});Q12=makeQuery(id+"F30.imprint","IMPRINT",FACE,{"disambiguationData":[TD([[makeQuery(id+"F30.imprint","IMPRINT",EDGE,{"disambiguationData":[TD([[subQ4,1.0]])],"derivedFrom":subQ3}),1.0]])]});}
            var Q13;
            Q13=makeQuery(id+"F30.imprint","IMPRINT",FACE,{"disambiguationData":[TD([[makeQuery(id+"F30.imprint","IMPRINT",EDGE,{"derivedFrom":sQuery(id+"F30.wireOp",EDGE,"E75")}),-1.0]])]});
            var Q14;
            {var subQ0=sQuery(id+"F30.wireOp",EDGE,"E74.right");var subQ1=sQuery(id+"F30.wireOp",EDGE,"E74.bottom");var subQ2=makeQuery(id+"F30.imprint","INTERSECT",VERTEX,{"derivedFrom":[subQ1,subQ0]});Q14=makeQuery(id+"F30.imprint","IMPRINT",FACE,{"disambiguationData":[TD([[makeQuery(id+"F30.imprint","IMPRINT",EDGE,{"disambiguationData":[TD([[subQ2,1.0]])],"derivedFrom":subQ1}),-1.0]])]});}
            var Q15;
            {var subQ0=sQuery(id+"F30.wireOp",EDGE,"E81");Q15=makeQuery(id+"F30.imprint","IMPRINT",FACE,{"disambiguationData":[TD([[makeQuery(id+"F30.imprint","IMPRINT",EDGE,{"derivedFrom":subQ0}),1.0]])]});}
            var Q16;
            {var subQ4=sQuery(id+"F30.wireOp",EDGE,"E91");Q16=makeQuery(id+"F30.imprint","IMPRINT",FACE,{"disambiguationData":[TD([[makeQuery(id+"F30.imprint","IMPRINT",EDGE,{"derivedFrom":subQ4}),1.0]])]});}
            var Q17;
            {var subQ0=sQuery(id+"F30.wireOp",EDGE,"E89");Q17=makeQuery(id+"F30.imprint","IMPRINT",FACE,{"disambiguationData":[TD([[makeQuery(id+"F30.imprint","IMPRINT",EDGE,{"derivedFrom":subQ0}),-1.0]])]});}
            var Q18;
            {var subQ2=sQuery(id+"F30.wireOp",EDGE,"E94");Q18=makeQuery(id+"F30.imprint","IMPRINT",FACE,{"disambiguationData":[TD([[makeQuery(id+"F30.imprint","IMPRINT",EDGE,{"derivedFrom":subQ2}),-1.0]])]});}
            var Q19;
            {var subQ4=sQuery(id+"F30.wireOp",EDGE,"E95");Q19=makeQuery(id+"F30.imprint","IMPRINT",FACE,{"disambiguationData":[TD([[makeQuery(id+"F30.imprint","IMPRINT",EDGE,{"derivedFrom":subQ4}),-1.0]])]});}
            var Q20;
            {var subQ0=sQuery(id+"F30.wireOp",EDGE,"E99");var subQ1=sQuery(id+"F30.wireOp",EDGE,"E75");var subQ2=makeQuery(id+"F30.imprint","INTERSECT",VERTEX,{"disambiguationData":[OD(0.0)],"derivedFrom":[subQ1,subQ0]});Q20=makeQuery(id+"F30.imprint","IMPRINT",FACE,{"disambiguationData":[TD([[makeQuery(id+"F30.imprint","IMPRINT",EDGE,{"disambiguationData":[TD([[subQ2,-1.0]])],"derivedFrom":subQ1}),1.0]])]});}
            var Q21;
            {var subQ0=sQuery(id+"F30.wireOp",EDGE,"E100");var subQ1=sQuery(id+"F30.wireOp",EDGE,"E75");var subQ2=makeQuery(id+"F30.imprint","INTERSECT",VERTEX,{"disambiguationData":[OD(0.0)],"derivedFrom":[subQ1,subQ0]});Q21=makeQuery(id+"F30.imprint","IMPRINT",FACE,{"disambiguationData":[TD([[makeQuery(id+"F30.imprint","IMPRINT",EDGE,{"disambiguationData":[TD([[subQ2,-1.0]])],"derivedFrom":subQ1}),-1.0]])]});}
            var Q22;
            {var subQ0=sQuery(id+"F30.wireOp",EDGE,"E101");var subQ1=sQuery(id+"F30.wireOp",EDGE,"E75");var subQ2=makeQuery(id+"F30.imprint","INTERSECT",VERTEX,{"disambiguationData":[OD(0.0)],"derivedFrom":[subQ1,subQ0]});Q22=makeQuery(id+"F30.imprint","IMPRINT",FACE,{"disambiguationData":[TD([[makeQuery(id+"F30.imprint","IMPRINT",EDGE,{"disambiguationData":[TD([[subQ2,1.0]])],"derivedFrom":subQ1}),-1.0]])]});}
            var Q23;
            {var subQ0=sQuery(id+"F30.wireOp",EDGE,"E102");var subQ1=sQuery(id+"F30.wireOp",EDGE,"E75");var subQ2=makeQuery(id+"F30.imprint","INTERSECT",VERTEX,{"disambiguationData":[OD(0.0)],"derivedFrom":[subQ1,subQ0]});Q23=makeQuery(id+"F30.imprint","IMPRINT",FACE,{"disambiguationData":[TD([[makeQuery(id+"F30.imprint","IMPRINT",EDGE,{"disambiguationData":[TD([[subQ2,-1.0]])],"derivedFrom":subQ1}),-1.0]])]});}
            var Q24;
            {var subQ0=sQuery(id+"F30.wireOp",EDGE,"E102");var subQ1=sQuery(id+"F30.wireOp",EDGE,"E75");var subQ2=makeQuery(id+"F30.imprint","INTERSECT",VERTEX,{"disambiguationData":[OD(0.0)],"derivedFrom":[subQ1,subQ0]});Q24=makeQuery(id+"F30.imprint","IMPRINT",FACE,{"disambiguationData":[TD([[makeQuery(id+"F30.imprint","IMPRINT",EDGE,{"disambiguationData":[TD([[subQ2,-1.0]])],"derivedFrom":subQ1}),1.0]])]});}
            var Q25;
            {var subQ0=sQuery(id+"F30.wireOp",EDGE,"E99");var subQ1=sQuery(id+"F30.wireOp",EDGE,"E75");var subQ2=makeQuery(id+"F30.imprint","INTERSECT",VERTEX,{"disambiguationData":[OD(0.0)],"derivedFrom":[subQ1,subQ0]});Q25=makeQuery(id+"F30.imprint","IMPRINT",FACE,{"disambiguationData":[TD([[makeQuery(id+"F30.imprint","IMPRINT",EDGE,{"disambiguationData":[TD([[subQ2,-1.0]])],"derivedFrom":subQ1}),-1.0]])]});}
            var Q26;
            {var subQ0=sQuery(id+"F30.wireOp",EDGE,"E100");var subQ1=sQuery(id+"F30.wireOp",EDGE,"E75");var subQ2=makeQuery(id+"F30.imprint","INTERSECT",VERTEX,{"disambiguationData":[OD(0.0)],"derivedFrom":[subQ1,subQ0]});Q26=makeQuery(id+"F30.imprint","IMPRINT",FACE,{"disambiguationData":[TD([[makeQuery(id+"F30.imprint","IMPRINT",EDGE,{"disambiguationData":[TD([[subQ2,-1.0]])],"derivedFrom":subQ1}),1.0]])]});}
            var Q27;
            {var subQ0=sQuery(id+"F30.wireOp",EDGE,"E101");var subQ1=sQuery(id+"F30.wireOp",EDGE,"E75");var subQ2=makeQuery(id+"F30.imprint","INTERSECT",VERTEX,{"disambiguationData":[OD(0.0)],"derivedFrom":[subQ1,subQ0]});Q27=makeQuery(id+"F30.imprint","IMPRINT",FACE,{"disambiguationData":[TD([[makeQuery(id+"F30.imprint","IMPRINT",EDGE,{"disambiguationData":[TD([[subQ2,1.0]])],"derivedFrom":subQ1}),1.0]])]});}
            extrude(context, id + "F31", {"entities" : qUnion([Q0, Q1, Q2, Q3, Q4, Q5, Q6, Q7, Q8, Q9, Q10, Q11, Q12, Q13, Q14, Q15, Q16, Q17, Q18, Q19, Q20, Q21, Q22, Q23, Q24, Q25, Q26, Q27]), "depth" : 3 * mm, "offsetDistance" : 25 * mm});
        }
        {
            var Q0;
            Q0=makeQuery(id+"F30.imprint","IMPRINT",FACE,{"disambiguationData":[TD([[makeQuery(id+"F30.imprint","IMPRINT",EDGE,{"derivedFrom":sQuery(id+"F30.wireOp",EDGE,"E76")}),1.0]])]});
            var Q1;
            Q1=makeQuery(id+"F30.imprint","IMPRINT",FACE,{"disambiguationData":[TD([[makeQuery(id+"F30.imprint","IMPRINT",EDGE,{"derivedFrom":sQuery(id+"F30.wireOp",EDGE,"E75")}),1.0]])]});
            extrude(context, id + "F32", {"entities" : qUnion([Q0, Q1]), "operationType" : NewBodyOperationType.ADD, "depth" : 25 * mm, "offsetDistance" : 25 * mm, "hasDraft" : true, "draftAngle" : 10 * degree});
        }
        {
            var Q0;
            Q0=makeQuery(id+"F30.imprint","IMPRINT",FACE,{"disambiguationData":[TD([[makeQuery(id+"F30.imprint","IMPRINT",EDGE,{"derivedFrom":sQuery(id+"F30.wireOp",EDGE,"E76")}),1.0]])]});
            extrude(context, id + "F33", {"entities" : qUnion([Q0]), "operationType" : NewBodyOperationType.REMOVE, "depth" : 25 * mm, "offsetDistance" : 25 * mm, "hasDraft" : true, "draftAngle" : 10 * degree});
        }
        {
            var Q0;
            {var subQ0=sQuery(id+"F30.wireOp",EDGE,"E74.top");Q0=makeQuery(id+"F30.imprint","IMPRINT",FACE,{"disambiguationData":[TD([[makeQuery(id+"F30.imprint","IMPRINT",EDGE,{"derivedFrom":subQ0}),1.0]])]});}
            var Q1;
            {var subQ0=sQuery(id+"F30.wireOp",EDGE,"E69.bottom");Q1=makeQuery(id+"F30.imprint","IMPRINT",FACE,{"disambiguationData":[TD([[makeQuery(id+"F30.imprint","IMPRINT",EDGE,{"derivedFrom":subQ0}),1.0]])]});}
            var Q2;
            {var subQ0=sQuery(id+"F30.wireOp",EDGE,"E74.right");var subQ1=sQuery(id+"F30.wireOp",EDGE,"E74.bottom");var subQ2=makeQuery(id+"F30.imprint","INTERSECT",VERTEX,{"derivedFrom":[subQ1,subQ0]});Q2=makeQuery(id+"F30.imprint","IMPRINT",FACE,{"disambiguationData":[TD([[makeQuery(id+"F30.imprint","IMPRINT",EDGE,{"disambiguationData":[TD([[subQ2,1.0]])],"derivedFrom":subQ1}),-1.0]])]});}
            var Q3;
            {var subQ0=sQuery(id+"F30.wireOp",EDGE,"E69.left");var subQ1=sQuery(id+"F30.wireOp",EDGE,"E69.top");var subQ2=makeQuery(id+"F30.imprint","INTERSECT",VERTEX,{"derivedFrom":[subQ1,subQ0]});Q3=makeQuery(id+"F30.imprint","IMPRINT",FACE,{"disambiguationData":[TD([[makeQuery(id+"F30.imprint","IMPRINT",EDGE,{"disambiguationData":[TD([[subQ2,-1.0]])],"derivedFrom":subQ1}),-1.0]])]});}
            var Q4;
            Q4=makeQuery(id+"F30.imprint","IMPRINT",FACE,{"disambiguationData":[TD([[makeQuery(id+"F30.imprint","IMPRINT",EDGE,{"derivedFrom":sQuery(id+"F30.wireOp",EDGE,"E74.left")}),1.0]])]});
            var Q5;
            {var subQ2=sQuery(id+"F30.wireOp",EDGE,"E94");Q5=makeQuery(id+"F30.imprint","IMPRINT",FACE,{"disambiguationData":[TD([[makeQuery(id+"F30.imprint","IMPRINT",EDGE,{"derivedFrom":subQ2}),-1.0]])]});}
            extrude(context, id + "F34", {"entities" : qUnion([Q0, Q1, Q2, Q3, Q4, Q5]), "operationType" : NewBodyOperationType.ADD, "oppositeDirection" : true, "depth" : 4 * mm, "offsetDistance" : 25 * mm});
        }
    });
